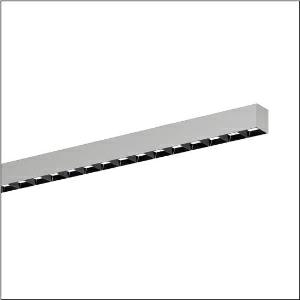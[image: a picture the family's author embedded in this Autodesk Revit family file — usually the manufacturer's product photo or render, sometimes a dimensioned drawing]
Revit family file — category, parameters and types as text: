
# Revit family: silica_r__21_51mx21dc4asb_ccd6
name_source: partatom
category: Lighting Fixtures
units: mm (PartAtom-declared; Revit-internal decimal feet)

## family parameters
Cut with Voids When Loaded = No
Host = Face
Light Source = No
Part Type = Normal
Room Calculation Point = No
Round Connector Dimension = Use Diameter
Shared = No

## types (1)
- --- (1 x LED, 10800 lm, 64.8 W, 4000K)
    Apparent Load = 65 VA
    CIE Flux Codes = 87 99 100 100 100
    Color Rendering = 80
    Color Temperature = 4000K
    Default Elevation = 1800 mm
    Description = Silica® 21, office luminaire, primary light control with darklight reflector, of PMMA, black, CAT 2 (L<= 3000cd/m²), light emission: direct distribution, primary light characteristic: symmetric, installation type: surface-mounted, LED, rated luminous flux: 10.800lm, luminous efficacy: 167lm/W, light colour: 840, colour temperature: 4000K, with terminal, 3+2-pole, max. 2.5mm², mains connection: 220..240V, AC, 50/60Hz, rated input power: 64.8W, luminaire housing, of aluminium, metallic grey (RAL 9006), length: 3.004mm, width: 53mm, height: 53mm, protection rating (complete): IP20, insulation class (complete): insulation class I (protective earthing), certification: CE, permissible operating ambient temperature: 0..+35°C, standard: EN 50419, packaging unit: 1 piece
    Height = 0 mm  [stored 0 ft]
    Lamp = 1 x LED
    Lamp Light Flux = 10800 lm
    Lamp Power = 64.8 W
    Lamp count = 1
    Length = 3004 mm
    Luminous efficacy = 167 lm/W
    Manufacturer = Siteco
    ModVariant = No
    Model = 51MX21DC4ASB
    Mounting Place = Ceiling
    Mounting Type = Recessed
    Number of Poles = 1
    OnlyDefault = Yes
    Power Factor = 1
    Product Name = Silica® 21
    Product group = office luminaire | ceiling recessed
    ProductGroupID = 400
    Protection Class = Protection class I
    Protection Degree = IP 20
    RLX_Detail_Level = 1
    RLX_Emergency_Light_Flux = 0 lm
    RLX_Emergency_Type = 0
    RLX_Emergency_Type_DB = No
    RlxData = <blob elided: 63681 chars, md5=460abab9>
    Socket = socket
    Standby Power = 0 W
    System Light Flux = 10800 lm
    System Power = 65 W
    Type Comments = factory setting: luminous flux: 100 % | dim-lin: 254 | 367 mA
    Type Image = l_1335929.jpg
    URL = http://relux.com
    VarID = @adj_093125
    Voltage = 0 V
    Weight = 0.00 kg
    Width = 53 mm

note: [stored X ft] marks values corroborated as IEEE doubles in the binary element streams (Revit-internal decimal feet)

## geometry (parser evidence)
native form markers: Blend x4, Sweep x11
no freeform markers — native parametric forms only
